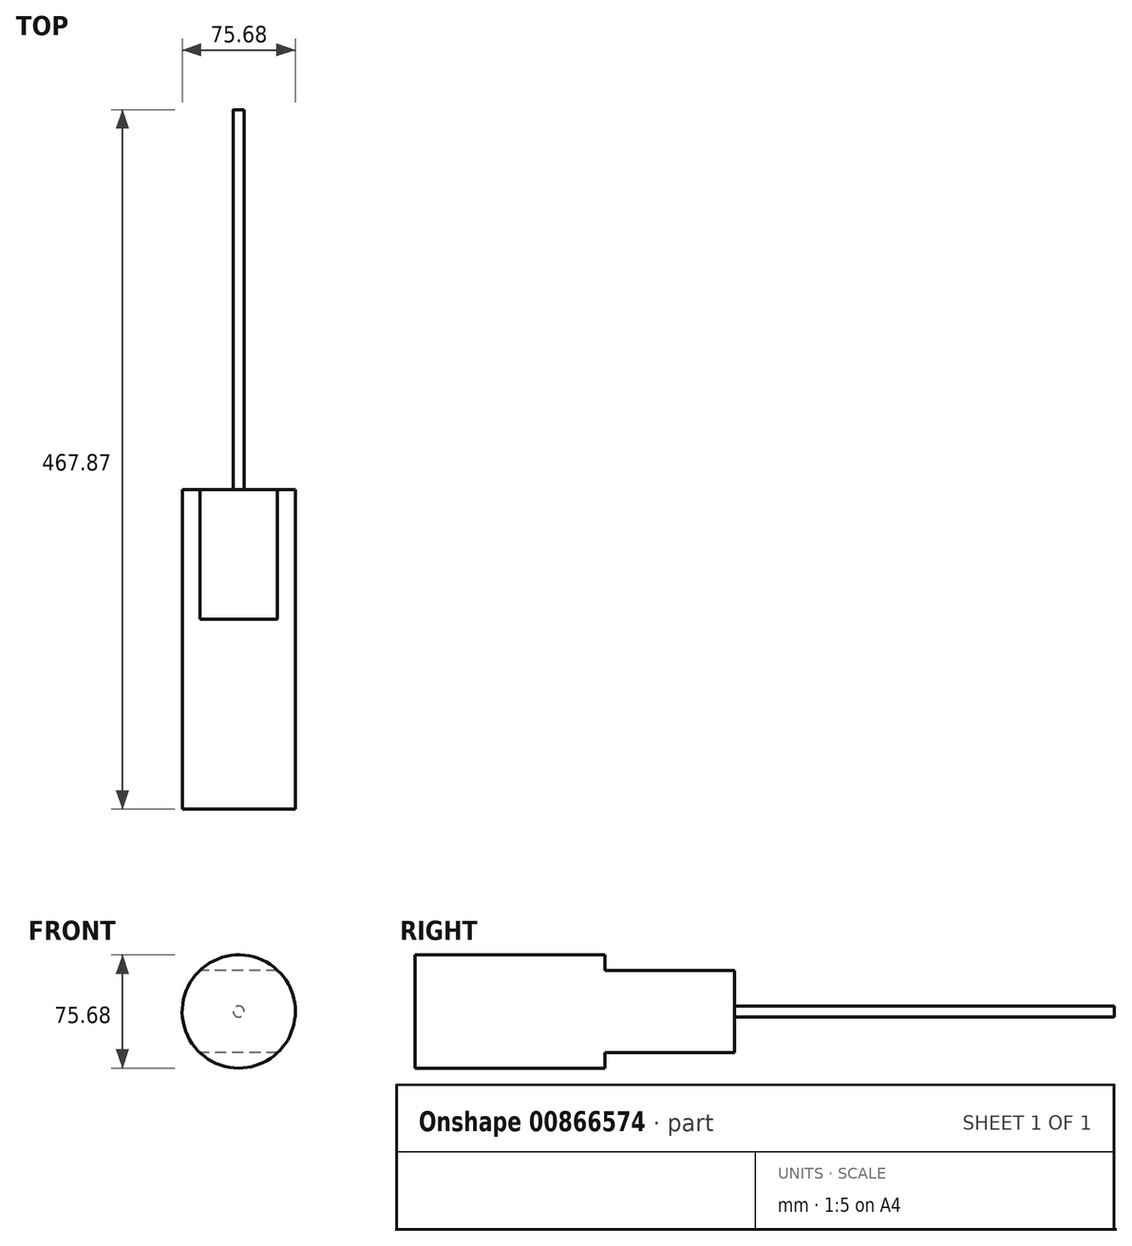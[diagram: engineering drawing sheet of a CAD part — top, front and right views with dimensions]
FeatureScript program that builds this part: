
annotation { "Feature Type Name" : "Feature", "Feature Type Description" : "" }
export const myFeature = defineFeature(function(context is Context, id is Id, definition is map)
    precondition{}
    {
        {
            var Q0;
            Q0=qCreatedBy(makeId("Front.planeOp"),FACE);
            var sketch = newSketch(context, id + "F0", { "sketchPlane" : qUnion([Q0])});
            skCircle(sketch, "E0", {"center": v(0, 0) * mm, "radius": 37.84 * mm});
            skSolve(sketch);
        }
        {
            var Q0;
            Q0=makeQuery(id+"F0.imprint","IMPRINT",FACE,{"disambiguationData":[TD([[makeQuery(id+"F0.imprint","IMPRINT",EDGE,{"derivedFrom":sQuery(id+"F0.wireOp",EDGE,"E0")}),1.0]])]});
            extrude(context, id + "F1", {"entities" : qUnion([Q0]), "depth" : 127 * mm, "offsetDistance" : 25.4 * mm});
        }
        {
            var Q0;
            Q0=makeQuery(id+"F1.opExtrude","CAP_FACE",FACE,{"disambiguationData":[OSD([sQuery(id+"F0.wireOp",EDGE,"E0")])],"isStart":true});
            var sketch = newSketch(context, id + "F2", { "sketchPlane" : qUnion([Q0])});
            skLineSegment(sketch, "E1.bottom", {"start": v(0, 0) * mm, "end": v(0, 0) * mm});
            skLineSegment(sketch, "E1.top", {"start": v(0, -27.41) * mm, "end": v(0, -27.41) * mm});
            skLineSegment(sketch, "E1.left", {"start": v(0, 0) * mm, "end": v(0, -27.41) * mm});
            skLineSegment(sketch, "E1.right", {"start": v(0, 0) * mm, "end": v(0, -27.41) * mm});
            skLineSegment(sketch, "E2.bottom", {"start": v(-43.64, -27.41) * mm, "end": v(45.88, -27.41) * mm});
            skLineSegment(sketch, "E2.top", {"start": v(-43.64, 27.52) * mm, "end": v(45.88, 27.52) * mm});
            skLineSegment(sketch, "E2.left", {"start": v(-43.64, -27.41) * mm, "end": v(-43.64, 27.52) * mm});
            skLineSegment(sketch, "E2.right", {"start": v(45.88, -27.41) * mm, "end": v(45.88, 27.52) * mm});
            skSolve(sketch);
        }
        {
            var Q0;
            {var subQ4=sQuery(id+"F2.wireOp",EDGE,"E2.bottom");var subQ5=makeQuery(id+"F2.imprint","IMPRINT",VERTEX,{"derivedFrom":subQ4});Q0=makeQuery(id+"F2.imprint","IMPRINT",FACE,{"disambiguationData":[TD([[makeQuery(id+"F2.imprint","IMPRINT",EDGE,{"disambiguationData":[TD([[subQ5,1.0]])],"derivedFrom":subQ4}),1.0]])]});}
            extrude(context, id + "F3", {"entities" : qUnion([Q0]), "operationType" : NewBodyOperationType.ADD, "depth" : 86.87 * mm, "offsetDistance" : 25.4 * mm});
        }
        {
            var Q0;
            Q0=makeQuery(id+"F3.opExtrude","CAP_FACE",FACE,{"disambiguationData":[OSD([sQuery(id+"F0.wireOp",EDGE,"E0"),sQuery(id+"F2.wireOp",EDGE,"E2.bottom"),sQuery(id+"F2.wireOp",EDGE,"E2.top")])],"isStart":false});
            var sketch = newSketch(context, id + "F4", { "sketchPlane" : qUnion([Q0])});
            skCircle(sketch, "E3", {"center": v(0, 0) * mm, "radius": 3.68 * mm});
            skSolve(sketch);
        }
        {
            var Q0;
            Q0=makeQuery(id+"F4.imprint","IMPRINT",FACE,{"disambiguationData":[TD([[makeQuery(id+"F4.imprint","IMPRINT",EDGE,{"derivedFrom":sQuery(id+"F4.wireOp",EDGE,"E3")}),1.0]])]});
            extrude(context, id + "F5", {"entities" : qUnion([Q0]), "operationType" : NewBodyOperationType.ADD, "depth" : 254 * mm, "offsetDistance" : 25.4 * mm});
        }
    });
